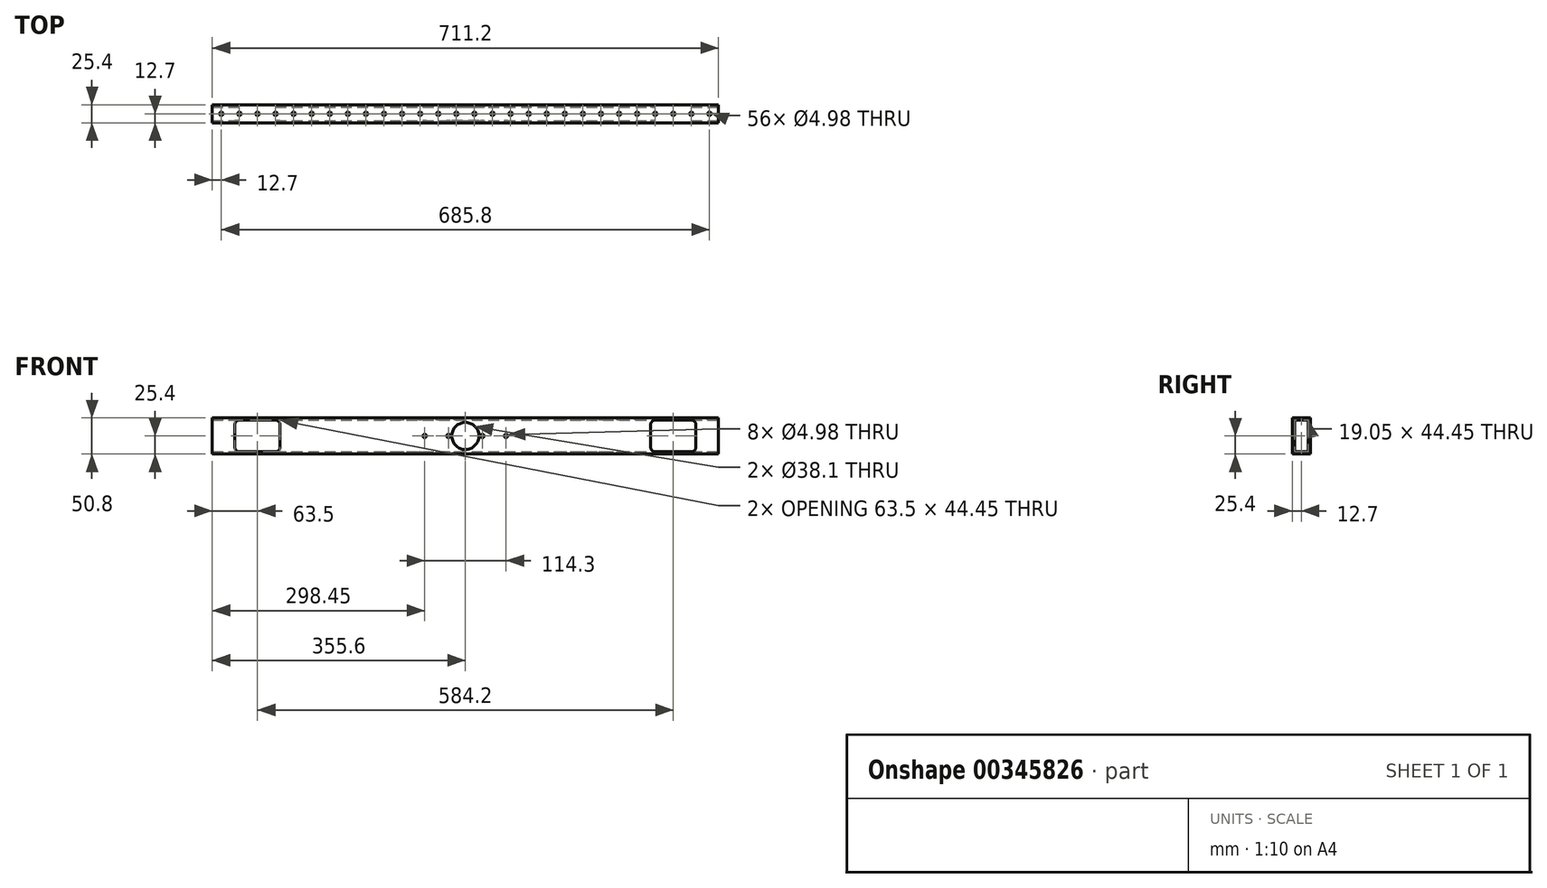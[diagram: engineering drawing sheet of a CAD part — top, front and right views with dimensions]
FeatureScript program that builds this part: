
annotation { "Feature Type Name" : "Feature", "Feature Type Description" : "" }
export const myFeature = defineFeature(function(context is Context, id is Id, definition is map)
    precondition{}
    {
        {
            var Q0;
            Q0=qCreatedBy(makeId("Top.planeOp"),FACE);
            var sketch = newSketch(context, id + "F0", { "sketchPlane" : qUnion([Q0])});
            skLineSegment(sketch, "E0.bottom", {"start": v(-355.6, 12.7) * mm, "end": v(355.6, 12.7) * mm});
            skLineSegment(sketch, "E0.top", {"start": v(-355.6, -12.7) * mm, "end": v(355.6, -12.7) * mm});
            skLineSegment(sketch, "E0.left", {"start": v(-355.6, 12.7) * mm, "end": v(-355.6, -12.7) * mm});
            skLineSegment(sketch, "E0.right", {"start": v(355.6, 12.7) * mm, "end": v(355.6, -12.7) * mm});
            skPoint(sketch, "E0.middle", {"position": v(0, 0) * mm});
            skSolve(sketch);
        }
        {
            var Q0;
            Q0=qSketchRegion(id+"F0",true);
            extrude(context, id + "F1", {"entities" : qUnion([Q0]), "endBound" : BoundingType.SYMMETRIC, "depth" : 50.8 * mm});
        }
        {
            var Q0;
            Q0=makeQuery(id+"F1.opExtrude","SWEPT_FACE",FACE,{"disambiguationData":[OSD([sQuery(id+"F0.wireOp",EDGE,"E0.right")])]});
            var sketch = newSketch(context, id + "F2", { "sketchPlane" : qUnion([Q0])});
            skLineSegment(sketch, "E1.0", {"start": v(-9.52, -22.23) * mm, "end": v(9.53, -22.23) * mm});
            skLineSegment(sketch, "E1.1", {"start": v(-9.52, 22.23) * mm, "end": v(-9.52, -22.22) * mm});
            skLineSegment(sketch, "E1.2", {"start": v(9.53, 22.23) * mm, "end": v(-9.52, 22.23) * mm});
            skLineSegment(sketch, "E1.3", {"start": v(9.53, -22.22) * mm, "end": v(9.53, 22.23) * mm});
            skSolve(sketch);
        }
        {
            var Q0;
            Q0=makeQuery(id+"F2.imprint","IMPRINT",FACE,{"disambiguationData":[TD([[makeQuery(id+"F2.imprint","IMPRINT",EDGE,{"derivedFrom":sQuery(id+"F2.wireOp",EDGE,"E1.0")}),1.0]])]});
            extrude(context, id + "F3", {"entities" : qUnion([Q0]), "operationType" : NewBodyOperationType.REMOVE, "endBound" : BoundingType.THROUGH_ALL, "oppositeDirection" : true, "depth" : 25.4 * mm});
        }
        {
            var Q0;
            Q0=makeQuery(id+"F1.opExtrude","CAP_FACE",FACE,{"disambiguationData":[OSD([sQuery(id+"F0.wireOp",EDGE,"E0.bottom"),sQuery(id+"F0.wireOp",EDGE,"E0.top"),sQuery(id+"F0.wireOp",EDGE,"E0.left"),sQuery(id+"F0.wireOp",EDGE,"E0.right")])],"isStart":false});
            var sketch = newSketch(context, id + "F4", { "sketchPlane" : qUnion([Q0])});
            skLineSegment(sketch, "E2", {"start": v(-355.6, 0) * mm, "end": v(355.6, 0) * mm, "construction": true});
            skCircle(sketch, "E3", {"center": v(-342.9, 0) * mm, "radius": 2.49 * mm});
            skCircle(sketch, "E4.1.0.0", {"center": v(-317.5, 0) * mm, "radius": 2.49 * mm});
            skCircle(sketch, "E4.2.0.0", {"center": v(-292.1, 0) * mm, "radius": 2.49 * mm});
            skCircle(sketch, "E4.3.0.0", {"center": v(-266.7, 0) * mm, "radius": 2.49 * mm});
            skCircle(sketch, "E4.4.0.0", {"center": v(-241.3, 0) * mm, "radius": 2.49 * mm});
            skCircle(sketch, "E4.5.0.0", {"center": v(-215.9, 0) * mm, "radius": 2.49 * mm});
            skCircle(sketch, "E4.6.0.0", {"center": v(-190.5, 0) * mm, "radius": 2.49 * mm});
            skCircle(sketch, "E4.7.0.0", {"center": v(-165.1, 0) * mm, "radius": 2.49 * mm});
            skCircle(sketch, "E4.8.0.0", {"center": v(-139.7, 0) * mm, "radius": 2.49 * mm});
            skCircle(sketch, "E4.9.0.0", {"center": v(-114.3, 0) * mm, "radius": 2.49 * mm});
            skCircle(sketch, "E4.10.0.0", {"center": v(-88.9, 0) * mm, "radius": 2.49 * mm});
            skCircle(sketch, "E4.11.0.0", {"center": v(-63.5, 0) * mm, "radius": 2.49 * mm});
            skCircle(sketch, "E4.12.0.0", {"center": v(-38.1, 0) * mm, "radius": 2.49 * mm});
            skCircle(sketch, "E4.13.0.0", {"center": v(-12.7, 0) * mm, "radius": 2.49 * mm});
            skCircle(sketch, "E4.14.0.0", {"center": v(12.7, 0) * mm, "radius": 2.49 * mm});
            skCircle(sketch, "E4.15.0.0", {"center": v(38.1, 0) * mm, "radius": 2.49 * mm});
            skCircle(sketch, "E4.16.0.0", {"center": v(63.5, 0) * mm, "radius": 2.49 * mm});
            skCircle(sketch, "E4.17.0.0", {"center": v(88.9, 0) * mm, "radius": 2.49 * mm});
            skCircle(sketch, "E4.18.0.0", {"center": v(114.3, 0) * mm, "radius": 2.49 * mm});
            skCircle(sketch, "E4.19.0.0", {"center": v(139.7, 0) * mm, "radius": 2.49 * mm});
            skCircle(sketch, "E4.20.0.0", {"center": v(165.1, 0) * mm, "radius": 2.49 * mm});
            skCircle(sketch, "E4.21.0.0", {"center": v(190.5, 0) * mm, "radius": 2.49 * mm});
            skCircle(sketch, "E4.22.0.0", {"center": v(215.9, 0) * mm, "radius": 2.49 * mm});
            skCircle(sketch, "E4.23.0.0", {"center": v(241.3, 0) * mm, "radius": 2.49 * mm});
            skCircle(sketch, "E4.24.0.0", {"center": v(266.7, 0) * mm, "radius": 2.49 * mm});
            skCircle(sketch, "E4.25.0.0", {"center": v(292.1, 0) * mm, "radius": 2.49 * mm});
            skCircle(sketch, "E4.26.0.0", {"center": v(317.5, 0) * mm, "radius": 2.49 * mm});
            skCircle(sketch, "E4.27.0.0", {"center": v(342.9, 0) * mm, "radius": 2.49 * mm});
            skCircle(sketch, "E4.28.0.0", {"center": v(368.3, 0) * mm, "radius": 2.49 * mm});
            skCircle(sketch, "E4.29.0.0", {"center": v(393.7, 0) * mm, "radius": 2.49 * mm});
            skLineSegment(sketch, "E4.direction1", {"start": v(-342.9, 0) * mm, "end": v(-317.5, 0) * mm, "construction": true});
            skSolve(sketch);
        }
        {
            var Q0;
            Q0=qSketchRegion(id+"F4",true);
            extrude(context, id + "F5", {"entities" : qUnion([Q0]), "operationType" : NewBodyOperationType.REMOVE, "endBound" : BoundingType.THROUGH_ALL, "oppositeDirection" : true, "depth" : 25.4 * mm});
        }
        {
            var Q0;
            Q0=makeQuery(id+"F1.opExtrude","SWEPT_FACE",FACE,{"disambiguationData":[OSD([sQuery(id+"F0.wireOp",EDGE,"E0.top")])]});
            var sketch = newSketch(context, id + "F6", { "sketchPlane" : qUnion([Q0])});
            skLineSegment(sketch, "E5", {"start": v(-292.1, -2.38) * mm, "end": v(292.1, -2.38) * mm, "construction": true});
            skLineSegment(sketch, "E6", {"start": v(0, 0) * mm, "end": v(0, -2.38) * mm, "construction": true});
            skPoint(sketch, "E6.endSnap0", {"position": v(0, -25.4) * mm});
            skCircle(sketch, "E7", {"center": v(-292.1, -2.38) * mm, "radius": 50.8 * mm, "construction": true});
            skCircle(sketch, "E8", {"center": v(0, 0) * mm, "radius": 50.8 * mm, "construction": true});
            skCircle(sketch, "E9", {"center": v(292.1, -2.38) * mm, "radius": 50.8 * mm, "construction": true});
            skLineSegment(sketch, "E10.bottom", {"start": v(-317.5, -22.23) * mm, "end": v(-266.7, -22.23) * mm});
            skLineSegment(sketch, "E10.top", {"start": v(-317.5, 22.23) * mm, "end": v(-266.7, 22.23) * mm});
            skLineSegment(sketch, "E10.left", {"start": v(-323.85, -15.88) * mm, "end": v(-323.85, 15.87) * mm});
            skLineSegment(sketch, "E10.right", {"start": v(-260.35, -15.88) * mm, "end": v(-260.35, 15.88) * mm});
            skPoint(sketch, "E10.middle", {"position": v(-292.1, 0) * mm});
            skLineSegment(sketch, "E11.bottom", {"start": v(266.7, 22.23) * mm, "end": v(317.5, 22.23) * mm});
            skLineSegment(sketch, "E11.top", {"start": v(266.7, -22.22) * mm, "end": v(317.5, -22.22) * mm});
            skLineSegment(sketch, "E11.left", {"start": v(260.35, 15.88) * mm, "end": v(260.35, -15.87) * mm});
            skLineSegment(sketch, "E11.right", {"start": v(323.85, 15.88) * mm, "end": v(323.85, -15.87) * mm});
            skPoint(sketch, "E11.middle", {"position": v(292.1, 0) * mm});
            skPoint(sketch, "E12.visualSharp", {"position": v(-323.85, 22.22) * mm});
            skArc(sketch, "E12.filletArc", {"start": v(-317.5, 22.23) * mm, "mid": v(-322, 20.37) * mm, "end": v(-323.85, 15.87) * mm});
            skPoint(sketch, "E13.visualSharp", {"position": v(-260.35, 22.22) * mm});
            skArc(sketch, "E13.filletArc", {"start": v(-260.35, 15.88) * mm, "mid": v(-262.2, 20.37) * mm, "end": v(-266.7, 22.23) * mm});
            skPoint(sketch, "E14.visualSharp", {"position": v(-260.35, -22.23) * mm});
            skArc(sketch, "E14.filletArc", {"start": v(-266.7, -22.23) * mm, "mid": v(-262.2, -20.37) * mm, "end": v(-260.35, -15.88) * mm});
            skPoint(sketch, "E15.visualSharp", {"position": v(-323.85, -22.23) * mm});
            skArc(sketch, "E15.filletArc", {"start": v(-323.85, -15.88) * mm, "mid": v(-322, -20.37) * mm, "end": v(-317.5, -22.23) * mm});
            skPoint(sketch, "E16.visualSharp", {"position": v(260.35, -22.22) * mm});
            skArc(sketch, "E16.filletArc", {"start": v(260.35, -15.87) * mm, "mid": v(262.2, -20.37) * mm, "end": v(266.7, -22.23) * mm});
            skPoint(sketch, "E17.visualSharp", {"position": v(260.35, 22.23) * mm});
            skArc(sketch, "E17.filletArc", {"start": v(266.7, 22.23) * mm, "mid": v(262.2, 20.37) * mm, "end": v(260.35, 15.88) * mm});
            skPoint(sketch, "E18.visualSharp", {"position": v(323.85, 22.23) * mm});
            skArc(sketch, "E18.filletArc", {"start": v(323.85, 15.88) * mm, "mid": v(322, 20.37) * mm, "end": v(317.5, 22.23) * mm});
            skPoint(sketch, "E19.visualSharp", {"position": v(323.85, -22.22) * mm});
            skArc(sketch, "E19.filletArc", {"start": v(317.5, -22.23) * mm, "mid": v(322, -20.37) * mm, "end": v(323.85, -15.87) * mm});
            skCircle(sketch, "E20", {"center": v(0, 0) * mm, "radius": 19.05 * mm});
            skLineSegment(sketch, "E21", {"start": v(-23.81, 0) * mm, "end": v(23.81, 0) * mm});
            skCircle(sketch, "E22", {"center": v(-23.81, 0) * mm, "radius": 2.49 * mm});
            skCircle(sketch, "E23", {"center": v(23.81, 0) * mm, "radius": 2.49 * mm});
            skCircle(sketch, "E24", {"center": v(-57.15, 0) * mm, "radius": 2.49 * mm});
            skCircle(sketch, "E25", {"center": v(57.15, 0) * mm, "radius": 2.49 * mm});
            skLineSegment(sketch, "E26", {"start": v(-57.15, 0) * mm, "end": v(57.15, 0) * mm, "construction": true});
            skSolve(sketch);
        }
        {
            var Q0;
            Q0 = qSketchRegion(id + "F6", true);
            extrude(context, id + "F7", {"entities" : qUnion([Q0]), "operationType" : NewBodyOperationType.REMOVE, "endBound" : BoundingType.THROUGH_ALL, "oppositeDirection" : true, "depth" : 25.4 * mm});
        }
    });
